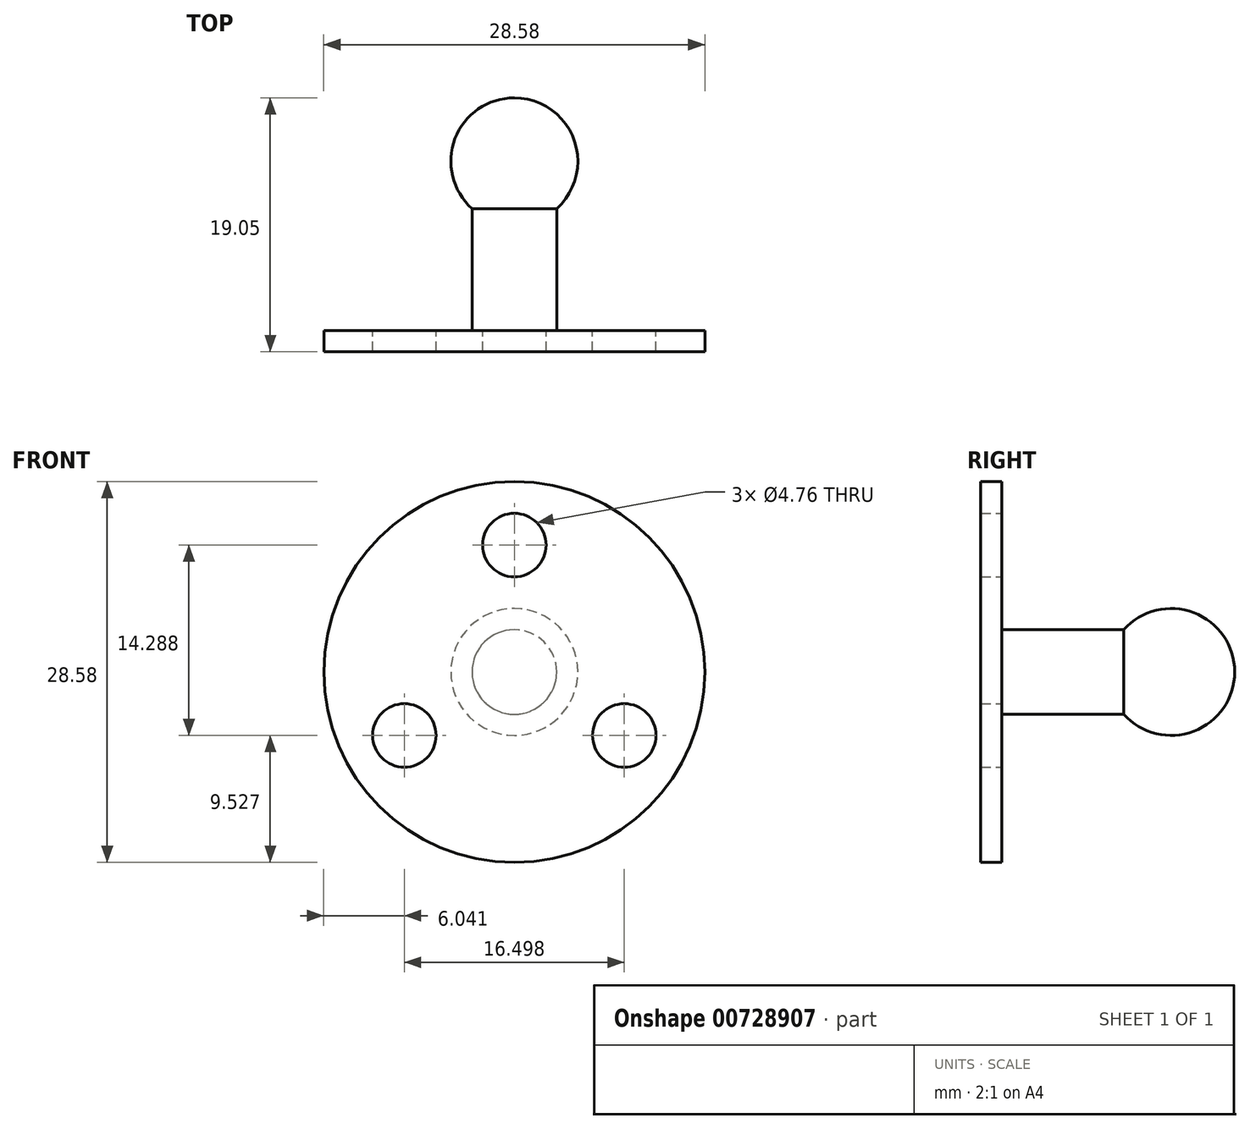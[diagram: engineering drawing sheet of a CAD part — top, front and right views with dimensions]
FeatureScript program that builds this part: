
annotation { "Feature Type Name" : "Feature", "Feature Type Description" : "" }
export const myFeature = defineFeature(function(context is Context, id is Id, definition is map)
    precondition{}
    {
        {
            var Q0;
            Q0=qCreatedBy(makeId("Front.planeOp"),FACE);
            var sketch = newSketch(context, id + "F0", { "sketchPlane" : qUnion([Q0])});
            skCircle(sketch, "E0", {"center": v(0, 0) * mm, "radius": 14.29 * mm});
            skCircle(sketch, "E1", {"center": v(0, 9.53) * mm, "radius": 2.38 * mm});
            skCircle(sketch, "E2.1.0", {"center": v(-8.25, -4.76) * mm, "radius": 2.38 * mm});
            skCircle(sketch, "E2.2.0", {"center": v(8.25, -4.76) * mm, "radius": 2.38 * mm});
            skSolve(sketch);
        }
        {
            var Q0;
            Q0=makeQuery(id+"F0.imprint","IMPRINT",FACE,{"disambiguationData":[TD([[makeQuery(id+"F0.imprint","IMPRINT",EDGE,{"derivedFrom":sQuery(id+"F0.wireOp",EDGE,"E0")}),1.0]])]});
            extrude(context, id + "F1", {"entities" : qUnion([Q0]), "depth" : 1.59 * mm, "offsetDistance" : 25.4 * mm});
        }
        {
            var Q0;
            Q0=qCreatedBy(makeId("Top.planeOp"),FACE);
            var sketch = newSketch(context, id + "F2", { "sketchPlane" : qUnion([Q0])});
            skLineSegment(sketch, "E3", {"start": v(3.18, 0) * mm, "end": v(3.18, 9.15) * mm});
            skArc(sketch, "E4", {"start": v(0, 7.94) * mm, "mid": v(4.76, 12.7) * mm, "end": v(0, 17.46) * mm});
            skLineSegment(sketch, "E5", {"start": v(0, 12.7) * mm, "end": v(0, 0) * mm});
            skLineSegment(sketch, "E6", {"start": v(0, 0) * mm, "end": v(3.18, 0) * mm});
            skLineSegment(sketch, "E7", {"start": v(0, 12.7) * mm, "end": v(0, 17.46) * mm});
            skPoint(sketch, "E8.orphan", {"position": v(3.18, 12.7) * mm});
            skSolve(sketch);
        }
        {
            var Q0;
            {var subQ0=sQuery(id+"F2.wireOp",EDGE,"E6");Q0=makeQuery(id+"F2.imprint","IMPRINT",FACE,{"disambiguationData":[TD([[makeQuery(id+"F2.imprint","IMPRINT",EDGE,{"derivedFrom":subQ0}),1.0]])]});}
            var Q1;
            {var subQ0=sQuery(id+"F2.wireOp",EDGE,"E4");var subQ1=makeQuery(id+"F2.imprint","INTERSECT",VERTEX,{"derivedFrom":[sQuery(id+"F2.wireOp",EDGE,"E3"),subQ0]});Q1=makeQuery(id+"F2.imprint","IMPRINT",FACE,{"disambiguationData":[TD([[makeQuery(id+"F2.imprint","IMPRINT",EDGE,{"disambiguationData":[TD([[subQ1,1.0]])],"derivedFrom":subQ0}),1.0]])]});}
            var Q2;
            Q2=sQuery(id+"F2.wireOp",EDGE,"E5");
            revolve(context, id + "F3", {"surfaceOperationType" : NewSurfaceOperationType.NEW, "entities" : qUnion([Q0, Q1]), "axis" : qUnion([Q2]), "revolveType" : RevolveType.FULL});
        }
    });
